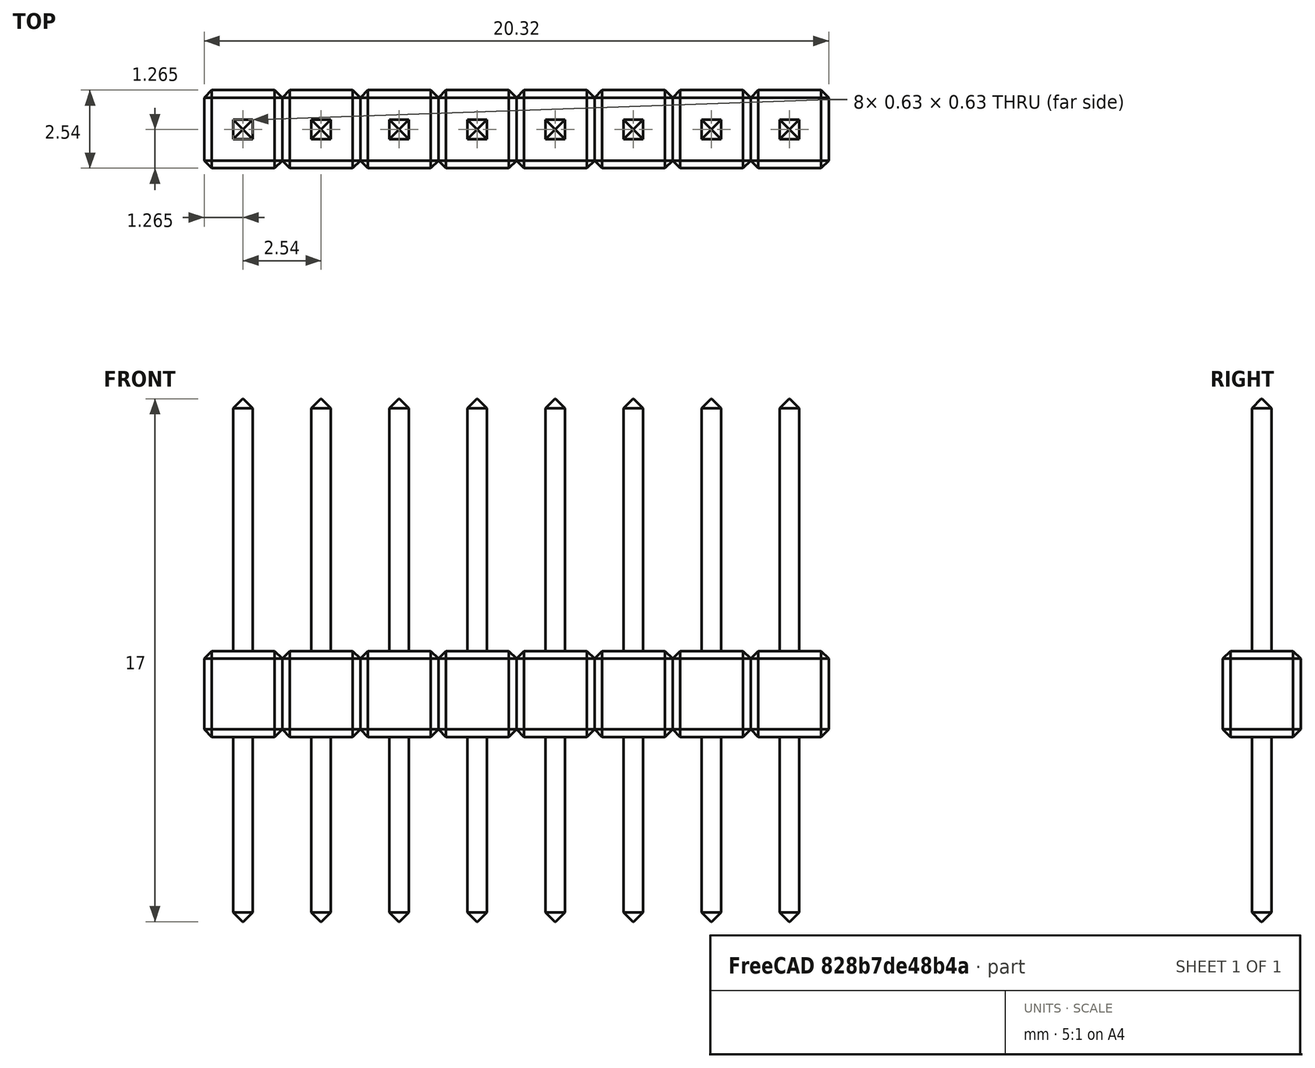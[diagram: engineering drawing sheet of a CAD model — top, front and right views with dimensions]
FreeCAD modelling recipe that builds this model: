
FCSTD DOCUMENT  (FreeCAD 0.18R4 (GitTag))
Label: 8 Pin Header
License: All rights reserved
LicenseURL: http://en.wikipedia.org/wiki/All_rights_reserved
objects: Part::Box×2, Part::Chamfer×2, Part::FeaturePython×2, Part::MultiFuse×1
note: 7 computed .brp shape members not serialized (recipe doc carries the construction recipe); baked Part::Feature solids carry a one-line shape summary decoded from their .brp

FEATURE [Part::Box] Box  label="Cube"
  AttacherType = Attacher::AttachEngine3D
  Height = 2.8
  Length = 2.54
  Width = 2.54
FEATURE [Part::Box] Box001  label="Cube001"
  AttacherType = Attacher::AttachEngine3D
  Height = 17
  Length = 0.63
  Placement = pos=(-3,0,0) rot=(0,0,1;0rad)
  Width = 0.63
FEATURE [Part::Chamfer] Chamfer  label="Body"
  Base = -> Box
  Edges = 12 edges r=0.25: [Edge1,Edge2,Edge3,Edge4,Edge5,Edge6,Edge7,Edge8,Edge9,Edge10,Edge11,Edge12]
FEATURE [Part::Chamfer] Chamfer001  label="Pin"
  Base = -> Box001
  Edges = 8 edges r=0.3: [Edge2,Edge4,Edge6,Edge8,Edge9,Edge10,Edge11,Edge12]
  Placement = pos=(3.95,0.95,-6) rot=(0,0,1;0rad)
FEATURE [Part::FeaturePython] Array  label="Bodies"  # Draft array (typed FeaturePython)
  Angle = 360
  ArrayType = 0
  Axis = (0,0,1)
  Base = -> Chamfer
  Center = (0,0,0)
  Fuse = false
  IntervalAxis = (0,0,0)
  IntervalX = (2.54,0,0)
  IntervalY = (0,1,0)
  IntervalZ = (0,0,1)
  NumberPolar = 1
  NumberX = 8
  NumberY = 1
  NumberZ = 1
FEATURE [Part::FeaturePython] Array001  label="Pins"  # Draft array (typed FeaturePython)
  Angle = 360
  ArrayType = 0
  Axis = (0,0,1)
  Base = -> Chamfer001
  Center = (0,0,0)
  Fuse = false
  IntervalAxis = (0,0,0)
  IntervalX = (2.54,0,0)
  IntervalY = (0,1,0)
  IntervalZ = (0,0,1)
  NumberPolar = 1
  NumberX = 8
  NumberY = 1
  NumberZ = 1
FEATURE [Part::MultiFuse] Fusion  label="Header"
  Shapes = -> [Array,Array001]
